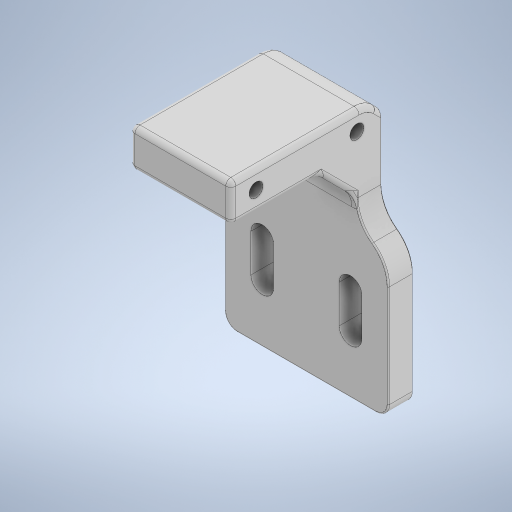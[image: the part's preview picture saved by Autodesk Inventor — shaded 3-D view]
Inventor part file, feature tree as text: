
AUTODESK INVENTOR PART (.ipt)
format: ipt  version: 2023 (Build 270158000, 158)  size: 446,464 bytes
history: native  units: mm
features: fillet x5, sketch x4, extrude x3, chamfer x3, projected_geometry x2, other x1, hole x1
ambient origin geometry x8: Origin, YZ Plane, XZ Plane, XY Plane, X Axis, Y Axis, Z Axis, Center Point
bodies: Body1 (feature_tree)
feature tree (19):
  other  "Těleso1"
  extrude  "Vysunutí1"  Depth=10.0mm TaperAngle=0.0deg
  extrude  "Vysunutí2"  Depth=40.0mm
  chamfer  "Zkosení1"  Distance=100.0mm
  chamfer  "Zkosení2"  Distance=55.0mm
  fillet  "Zaoblení1"  Radius=12.5mm
  fillet  "Zaoblení2"  Radius=15.0mm
  fillet  "Zaoblení3"  Radius=50.0mm
  fillet  "Zaoblení4"  Radius=15.0mm
  extrude  "Vysunutí3"  Depth=5.0mm TaperAngle=45.0deg
  fillet  "Zaoblení5"  Radius=15.0mm
  hole  "Díra1"  [1 undecoded]
  chamfer  "Zkosení3"  Distance=0.5mm
  sketch  "Náčrt1"
  sketch  "Náčrt2"
  projected_geometry  "Promítnutá smyčka1"
  sketch  "Náčrt3"
  projected_geometry  "Promítnutá smyčka2"
  sketch  "Náčrt4"
note: 1 required parameter value undecoded (feature->parameter linkage not recoverable at this tier; creation-order binding heuristic only, values carry confidence <= 0.55)
